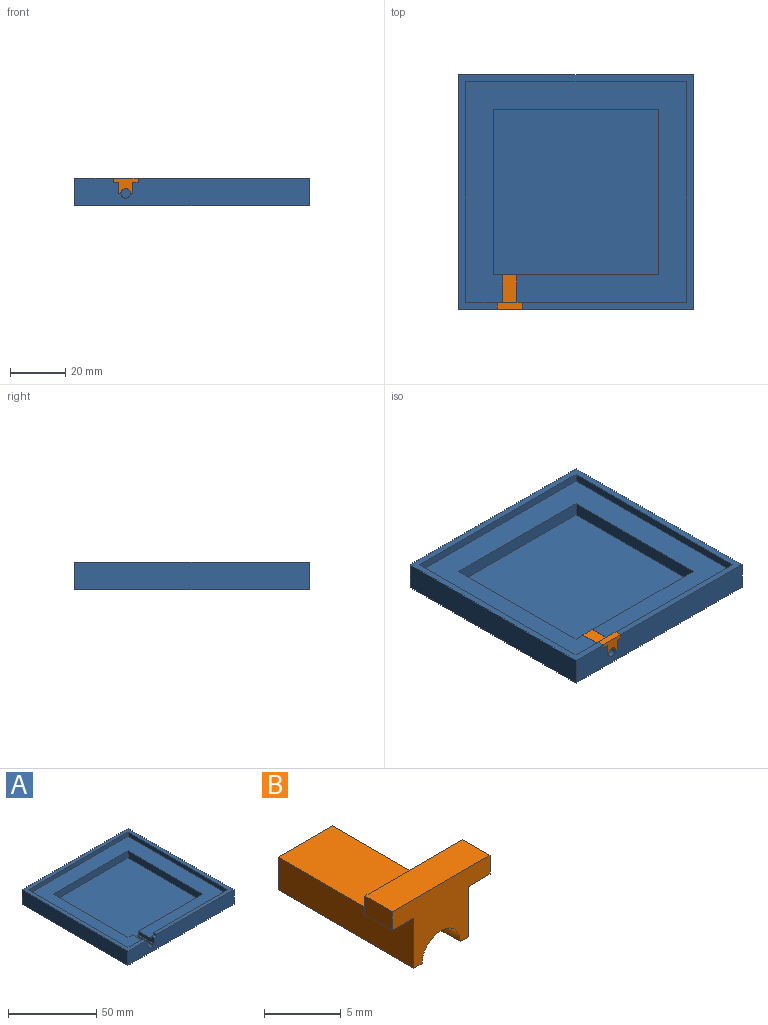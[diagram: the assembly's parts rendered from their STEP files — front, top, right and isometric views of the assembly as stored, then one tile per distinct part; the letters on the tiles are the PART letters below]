
ASSEMBLY  parts=2 mates=1
PART A: 26 faces, bbox 85x85x10 mm
  f0: plane 61.49x3mm, normal (0,1,0), area 181.5mm2, adj f2,f5,f15,f18,f20,f22
  f1: plane 85x10mm, normal (0,-1,0), area 811.7mm2, adj f2,f7,f8,f10,f17,f18,f19,f20
  f2: plane 85x85mm, normal (0,0,1), area 802.5mm2, adj f0,f1,f3,f4,f5,f6,f7,f8
  f3: plane 80x3mm, normal (1,0,0), area 240mm2, adj f2,f4,f6,f15
  f4: plane 13.51x3mm, normal (0,1,0), area 37.5mm2, adj f2,f3,f15,f17,f19,f21
  f5: plane 80x3mm, normal (-1,0,0), area 240mm2, adj f0,f2,f6,f15
  f6: plane 80x3mm, normal (0,-1,0), area 240mm2, adj f2,f3,f5,f15
  f7: plane 85x10mm, normal (-1,0,0), area 850mm2, adj f1,f2,f9,f10
  f8: plane 85x10mm, normal (1,0,0), area 850mm2, adj f1,f2,f9,f10
  f9: plane 85x10mm, normal (0,1,0), area 850mm2, adj f2,f7,f8,f10
  f10: plane 85x85mm, normal (0,0,-1), area 7225mm2, adj f1,f7,f8,f9
  f11: plane 60x5mm, normal (1,0,0), area 300mm2, adj f12,f14,f15,f16
  f12: plane 60x5mm, normal (0,-1,0), area 300mm2, adj f11,f13,f15,f16
  f13: plane 60x5mm, normal (-1,0,0), area 300mm2, adj f12,f14,f15,f16
  f14: plane 60x5mm, normal (0,1,0), area 282.7mm2, adj f11,f13,f15,f16,f21,f22,f23,f24
  f15: plane 80x80mm, normal (0,0,1), area 2750mm2, adj f0,f3,f4,f5,f6,f11,f12,f13
  f16: plane 60x60mm, normal (0,0,1), area 3600mm2, adj f11,f12,f13,f14
  f17: plane 2.5x2mm, normal (0,0,1), area 5mm2, adj f1,f4,f19,f21
  f18: plane 2.5x2mm, normal (0,0,1), area 5mm2, adj f0,f1,f20,f22
  f19: plane 2.5x1.5mm, normal (1,0,0), area 3.8mm2, adj f1,f2,f4,f17
  f20: plane 2.5x1.5mm, normal (-1,0,0), area 3.8mm2, adj f0,f1,f2,f18
  f21: plane 12.5x4mm, normal (1,0,0), area 35mm2, adj f1,f4,f14,f15,f17,f23
  f22: plane 12.5x4mm, normal (-1,0,0), area 35mm2, adj f0,f1,f14,f15,f18,f25
  f23: plane 12.5x0.75mm, normal (0,0,1), area 9.4mm2, adj f1,f14,f21,f24
  f24: cylinder r=1.75mm len=12.5mm, axis (0,-1,0), area 68.7mm2, adj f1,f14,f23,f25
  f25: plane 12.5x0.75mm, normal (0,0,1), area 9.4mm2, adj f1,f14,f22,f24
PART B: 14 faces, bbox 9x12.5x5.5 mm
  f0: plane 9x2.9mm, normal (0,1,0), area 20.5mm2, adj f1,f2,f7,f8,f9,f10,f11,f12
  f1: plane 12.5x4mm, normal (-1,0,0), area 36mm2, adj f0,f3,f6,f11,f12,f13
  f2: plane 12.5x4mm, normal (1,0,0), area 36mm2, adj f0,f5,f6,f8,f12,f13
  f3: plane 12.5x0.75mm, normal (0,0,-1), area 9.4mm2, adj f1,f4,f6,f13
  f4: cylinder r=1.75mm len=12.5mm, axis (0,1,0), area 68.7mm2, adj f3,f5,f6,f13
  f5: plane 12.5x0.75mm, normal (0,0,-1), area 9.4mm2, adj f2,f4,f6,f13
  f6: plane 9x5.5mm, normal (0,-1,0), area 28.7mm2, adj f1,f2,f3,f4,f5,f7,f8,f9
  f7: plane 9x2.5mm, normal (0,0,1), area 22.5mm2, adj f0,f6,f9,f10
  f8: plane 2.5x2mm, normal (0,0,-1), area 5mm2, adj f0,f2,f6,f9
  f9: plane 2.5x1.5mm, normal (1,0,0), area 3.8mm2, adj f0,f6,f7,f8
  f10: plane 2.5x1.5mm, normal (-1,0,0), area 3.8mm2, adj f0,f6,f7,f11
  f11: plane 2.5x2mm, normal (0,0,-1), area 5mm2, adj f0,f1,f6,f10
  f12: plane 10x5mm, normal (0,0,1), area 50mm2, adj f0,f1,f2,f13
  f13: plane 5x2.6mm, normal (0,1,0), area 8.2mm2, adj f1,f2,f3,f4,f5,f12
PLACE A t=(31.14,21.44,49.32)mm
PLACE B t=(7.15,-18.56,60.32)mm
MATE revolute B.f4 <-> A.f24  axis (0,-1,0) through (7.15,-21.06,53.82)mm
